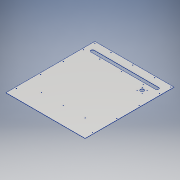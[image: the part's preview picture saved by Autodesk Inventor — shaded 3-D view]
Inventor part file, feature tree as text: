
AUTODESK INVENTOR PART (.ipt)
format: ipt  version: 2019 (Build 230136000, 136)  size: 231,424 bytes
history: native  units: mm
features: other x3, sketch x2, sheet_metal_op x1
ambient origin geometry x8: Origin, YZ Plane, XZ Plane, XY Plane, X Axis, Y Axis, Z Axis, Center Point
bodies: Body1 (feature_tree)
feature tree (6):
  sheet_metal_op  "Face3"
  sketch  "Sketch1"  dims[d0=490.0mm]
  other  "Plate3"
  sketch  "Sketch2"  dims[d1=550.0mm d2=10.0mm d3=10.0mm d4=10.0mm d5=110.0mm d6=80.0mm d7=110.0mm d8=110.0mm d9=70.0mm d10=55.0mm d11=4.2mm d12=0.8mm d13=0.8mm d14=42.0mm d15=15.0mm d16=50.0mm d17=31.0mm d18=3.4mm d19=22.0mm d20=0.8mm d21=1.5mm d23=20.0mm d24=400.0mm d25=1.5mm d26=0.0mm d28=10.5mm]
  other  "Cut1"
  other  "Definition1"
